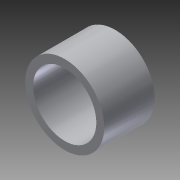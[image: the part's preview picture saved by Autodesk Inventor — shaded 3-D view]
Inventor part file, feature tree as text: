
AUTODESK INVENTOR PART (.ipt)
format: ipt  version: 2013 (Build 170138000, 138)  size: 83,456 bytes
history: native  units: in
note: dims shown in document units (in); Inventor stores cm internally (conversion verified against a paired STEP export)
features: extrude x1, sketch x1
ambient origin geometry x8: Origin, YZ Plane, XZ Plane, XY Plane, X Axis, Y Axis, Z Axis, Center Point
bodies: Solid1 (feature_tree)
feature tree (2):
  extrude  "Extrusion1"  Depth=0.625in
  sketch  "Sketch1"  dims[d0=0.5in d1=0.625in d2=0.4in d3=0.0in]
